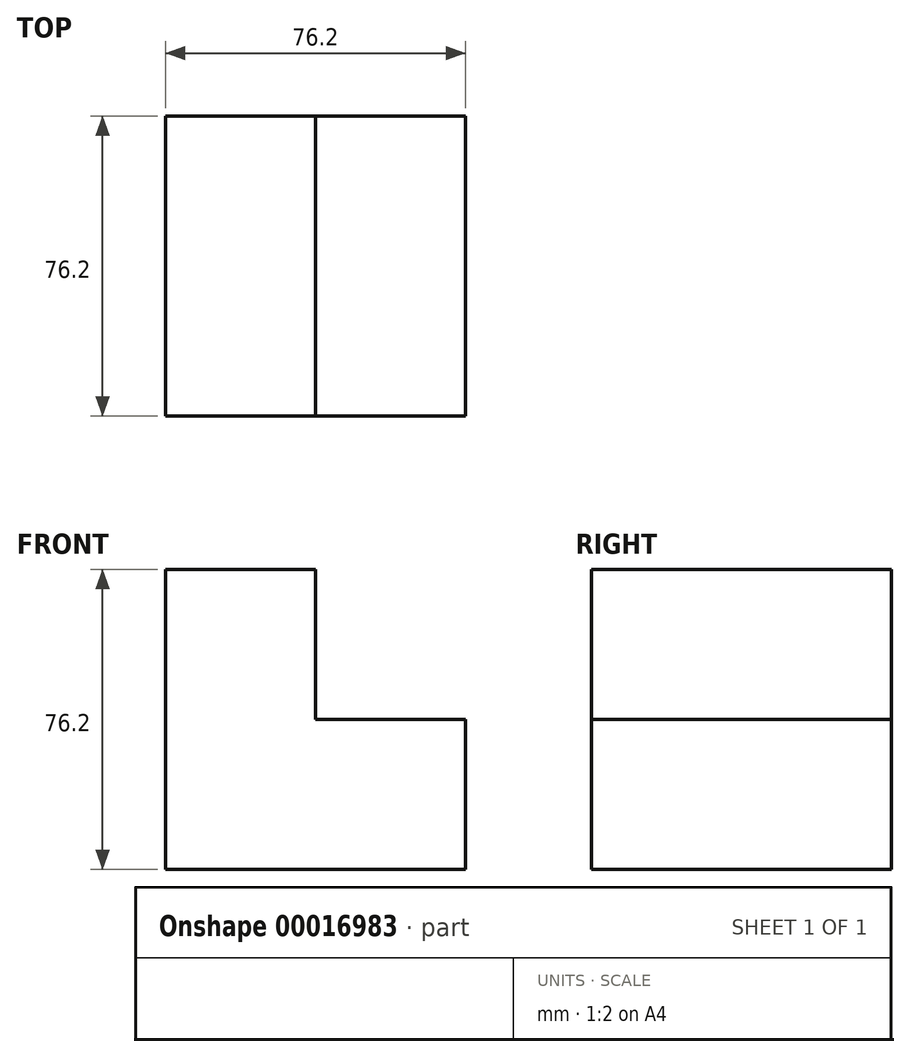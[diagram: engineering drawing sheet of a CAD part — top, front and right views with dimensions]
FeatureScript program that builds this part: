
annotation { "Feature Type Name" : "Feature", "Feature Type Description" : "" }
export const myFeature = defineFeature(function(context is Context, id is Id, definition is map)
    precondition{}
    {
        {
            var Q0;
            Q0=qCreatedBy(makeId("Front.planeOp"),FACE);
            var sketch = newSketch(context, id + "F0", { "sketchPlane" : qUnion([Q0])});
            skLineSegment(sketch, "E0", {"start": v(-51.71, 41.38) * mm, "end": v(-51.71, -34.82) * mm});
            skLineSegment(sketch, "E1", {"start": v(-51.71, -34.82) * mm, "end": v(24.49, -34.82) * mm});
            skLineSegment(sketch, "E2", {"start": v(24.49, -34.82) * mm, "end": v(24.49, 3.28) * mm});
            skLineSegment(sketch, "E3", {"start": v(24.49, 3.28) * mm, "end": v(-13.61, 3.28) * mm});
            skLineSegment(sketch, "E4", {"start": v(-13.61, 3.28) * mm, "end": v(-13.61, 41.38) * mm});
            skLineSegment(sketch, "E5", {"start": v(-13.61, 41.38) * mm, "end": v(-51.71, 41.38) * mm});
            skSolve(sketch);
        }
        {
            var Q0;
            Q0=makeQuery(id+"F0.imprint","IMPRINT",FACE,{"disambiguationData":[TD([[makeQuery(id+"F0.imprint","IMPRINT",EDGE,{"derivedFrom":sQuery(id+"F0.wireOp",EDGE,"E0")}),1.0]])]});
            extrude(context, id + "F1", {"entities" : qUnion([Q0]), "depth" : 76.2 * mm});
        }
    });
